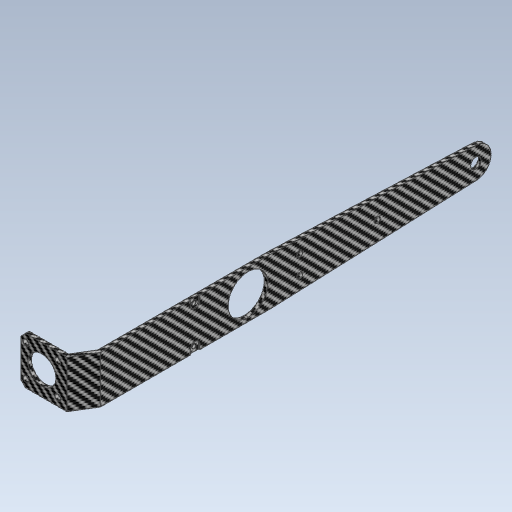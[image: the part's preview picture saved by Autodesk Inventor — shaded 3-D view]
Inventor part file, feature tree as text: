
AUTODESK INVENTOR PART (.ipt)
format: ipt  version: 2024 (Build 280153000, 153)  size: 207,360 bytes
history: native  units: mm
features: other x4, chamfer x2, extrude x1, sketch x1
ambient origin geometry x8: Origin, YZ Plane, XZ Plane, XY Plane, X Axis, Y Axis, Z Axis, Center Point
bodies: Body1 (feature_tree)
feature tree (8):
  other  "_bridseye_sketch.ipt"
  chamfer  "面取り1"  Distance=10.0mm
  chamfer  "面取り2"  Distance=0.5mm Angle=45.0deg
  extrude  "押し出し1"  Depth=2.0mm TaperAngle=45.0deg
  other  "ソリッド24::_bridseye_sketch.ipt"
  other  "TaggingFeature2"
  other  "side_links-link2"
  sketch  "スケッチ2"
